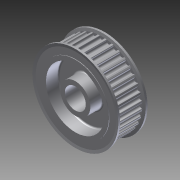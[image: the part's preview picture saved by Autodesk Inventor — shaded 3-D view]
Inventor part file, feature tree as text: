
AUTODESK INVENTOR PART (.ipt)
format: ipt  version: 2014 SP1 (Build 180222100, 222)  size: 1,040,896 bytes
history: native  units: in
note: dims shown in document units (in); Inventor stores cm internally (conversion verified against a paired STEP export)
features: mirror x1, other x1, imported_body x1
ambient origin geometry x8: Origin, YZ Plane, XZ Plane, XY Plane, X Axis, Y Axis, Z Axis, Center Point
bodies: Body1 (feature_tree)
feature tree (3):
  mirror  "Mirror1"
  other  "217-3232-STEP1"
  imported_body  "Base1"
